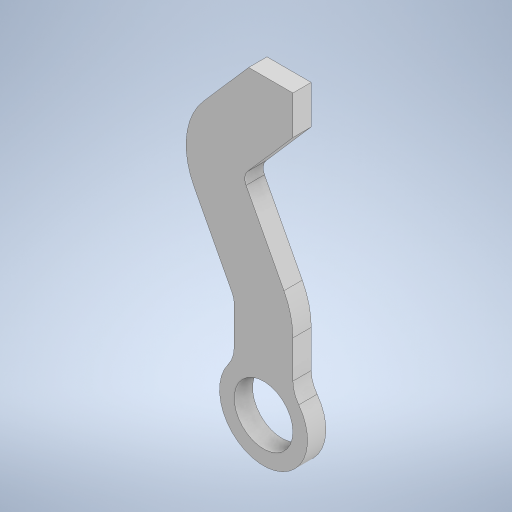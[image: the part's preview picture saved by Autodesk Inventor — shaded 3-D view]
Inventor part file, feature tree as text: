
AUTODESK INVENTOR PART (.ipt)
format: ipt  version: 2023.2 (Build 272271000, 271)  size: 272,896 bytes
history: native  units: mm
features: extrude x1, sketch x1
ambient origin geometry x8: Origin, YZ Plane, XZ Plane, XY Plane, X Axis, Y Axis, Z Axis, Center Point
bodies: Solid1 (feature_tree)
feature tree (2):
  extrude  "Extrusion1"  Depth=2.5mm TaperAngle=0.0deg
  sketch  "Sketch1"  dims[d1=8.0mm d2=2.5mm d3=0.0mm d4=12.0mm d5=30.0deg d6=19.198622mm d7=12.0mm d8=0.0mm d9=10.0mm d12=8.0mm d16=8.0mm d17=8.0mm d18=25.0mm d19=4.0mm d20=2.0mm d21=2.800309mm d22=13.393556mm d23=1.979367mm d24=28.288784mm d25=0.0mm]
